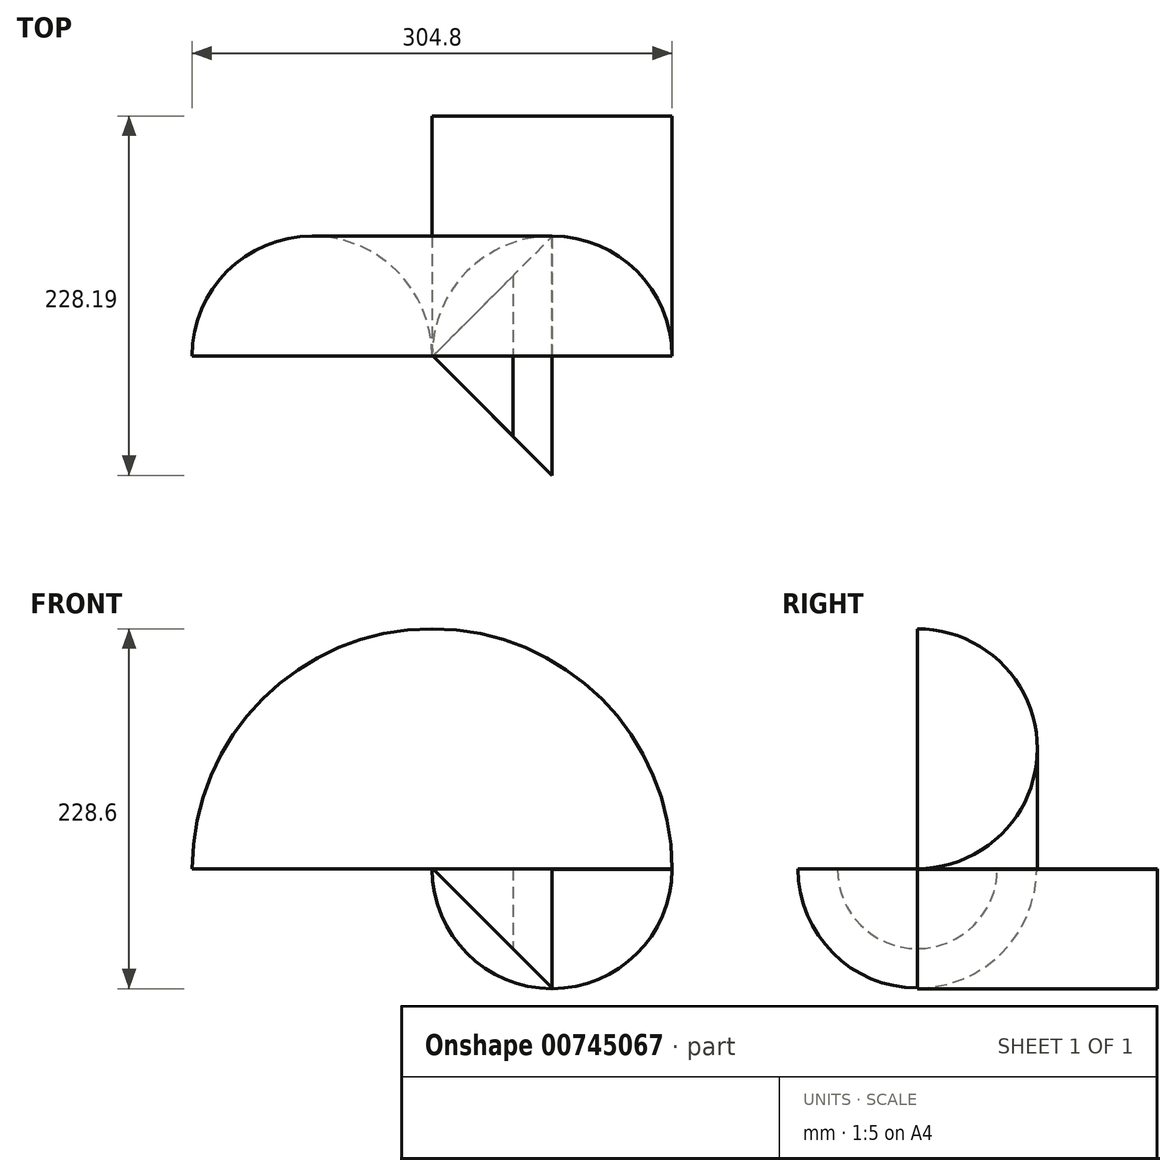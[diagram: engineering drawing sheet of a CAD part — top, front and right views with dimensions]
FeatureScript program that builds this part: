
annotation { "Feature Type Name" : "Feature", "Feature Type Description" : "" }
export const myFeature = defineFeature(function(context is Context, id is Id, definition is map)
    precondition{}
    {
        {
            var Q0;
            Q0=qCreatedBy(makeId("Top.planeOp"),FACE);
            var sketch = newSketch(context, id + "F0", { "sketchPlane" : qUnion([Q0])});
            skLineSegment(sketch, "E0", {"start": v(76.2, 0) * mm, "end": v(0, 0) * mm});
            skLineSegment(sketch, "E1", {"start": v(0, 0) * mm, "end": v(-76.2, 0) * mm});
            skArc(sketch, "E2", {"start": v(76.2, 0) * mm, "mid": v(0, 76.2) * mm, "end": v(-76.2, 0) * mm});
            skLineSegment(sketch, "E3", {"start": v(-76.2, 0) * mm, "end": v(-76.2, -78.48) * mm});
            skArc(sketch, "E4", {"start": v(-76.2, 0) * mm, "mid": v(0, -76.2) * mm, "end": v(76.2, 0) * mm});
            skCircle(sketch, "E5", {"center": v(-76.2, 0) * mm, "radius": 152.4 * mm});
            skSolve(sketch);
        }
        {
            var Q0;
            Q0=qCreatedBy(makeId("Front.planeOp"),FACE);
            var sketch = newSketch(context, id + "F1", { "sketchPlane" : qUnion([Q0])});
            skLineSegment(sketch, "E6", {"start": v(0, 0) * mm, "end": v(0, 76.2) * mm});
            skArc(sketch, "E7", {"start": v(-76.2, -0.2) * mm, "mid": v(-0.14, -76.2) * mm, "end": v(76.2, -0.48) * mm});
            skLineSegment(sketch, "E8", {"start": v(-76.2, -0.2) * mm, "end": v(76.2, -0.48) * mm});
            skSolve(sketch);
        }
        {
            var Q0;
            Q0=qCreatedBy(makeId("Top.planeOp"),FACE);
            var sketch = newSketch(context, id + "F2", { "sketchPlane" : qUnion([Q0])});
            skLineSegment(sketch, "E9", {"start": v(-75.56, 0) * mm, "end": v(0, -75.79) * mm});
            skLineSegment(sketch, "E10", {"start": v(-75.56, 0) * mm, "end": v(0, 0) * mm});
            skLineSegment(sketch, "E11", {"start": v(0, 0) * mm, "end": v(0, -75.79) * mm});
            skSolve(sketch);
        }
        {
            var Q0;
            Q0=makeQuery(id+"F2.imprint","IMPRINT",FACE,{"disambiguationData":[TD([[makeQuery(id+"F2.imprint","IMPRINT",EDGE,{"derivedFrom":sQuery(id+"F2.wireOp",EDGE,"E9")}),1.0]])]});
            var Q1;
            Q1=sQuery(id+"FNdkq6l8hAp5vaf_0.wireOp",EDGE,"w7kG1nW4-rzTr-gFp6-rHjN-6y3AfUU78O8H");
            var Q2;
            Q2=sQuery(id+"F0.wireOp",EDGE,"E0");
            revolve(context, id + "F3", {"surfaceOperationType" : NewSurfaceOperationType.NEW, "entities" : qUnion([Q0]), "surfaceEntities" : qUnion([Q1]), "axis" : qUnion([Q2]), "revolveType" : RevolveType.ONE_DIRECTION, "oppositeDirection" : true, "angle" : 180 * degree});
        }
        {
            var Q0;
            Q0=makeQuery(id+"F0.imprint","IMPRINT",FACE,{"disambiguationData":[TD([[makeQuery(id+"F0.imprint","IMPRINT",EDGE,{"derivedFrom":sQuery(id+"F0.wireOp",EDGE,"E0")}),-1.0]])]});
            var Q1;
            Q1=sQuery(id+"F0.wireOp",EDGE,"E2");
            var Q2;
            Q2=sQuery(id+"F0.wireOp",EDGE,"E3");
            revolve(context, id + "F4", {"surfaceOperationType" : NewSurfaceOperationType.NEW, "entities" : qUnion([Q0]), "surfaceEntities" : qUnion([Q1]), "axis" : qUnion([Q2]), "revolveType" : RevolveType.ONE_DIRECTION, "angle" : 180 * degree});
        }
        {
            var Q0;
            {var subQ2=sQuery(id+"F1.wireOp",EDGE,"E7");Q0=makeQuery(id+"F1.imprint","IMPRINT",FACE,{"disambiguationData":[TD([[makeQuery(id+"F1.imprint","IMPRINT",EDGE,{"derivedFrom":subQ2}),1.0]])]});}
            var Q1;
            Q1=sQuery(id+"F1.wireOp",EDGE,"408d1dcc-7add-44d6-a223-ddcf5036ed68");
            extrude(context, id + "F5", {"entities" : qUnion([Q0]), "surfaceEntities" : qUnion([Q1]), "oppositeDirection" : true, "depth" : 152.4 * mm, "offsetDistance" : 25.4 * mm});
        }
        {
            var Q0;
            Q0=qCreatedBy(makeId("Top.planeOp"),FACE);
            var sketch = newSketch(context, id + "F6", { "sketchPlane" : qUnion([Q0])});
            skLineSegment(sketch, "E12", {"start": v(-75.56, 0) * mm, "end": v(-24.76, 0) * mm});
            skLineSegment(sketch, "E13", {"start": v(-24.76, -50.8) * mm, "end": v(-24.76, 0) * mm});
            skLineSegment(sketch, "E14", {"start": v(-24.76, -50.8) * mm, "end": v(-75.56, 0) * mm});
            skSolve(sketch);
        }
        {
            var Q0;
            Q0 = qSketchRegion(id + "F6", true);
            var Q1;
            Q1=sQuery(id+"F2.wireOp",EDGE,"E10");
            revolve(context, id + "F7", {"surfaceOperationType" : NewSurfaceOperationType.NEW, "entities" : qUnion([Q0]), "axis" : qUnion([Q1]), "revolveType" : RevolveType.ONE_DIRECTION, "angle" : 180 * degree});
        }
    });
